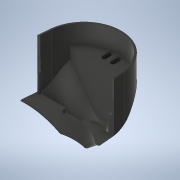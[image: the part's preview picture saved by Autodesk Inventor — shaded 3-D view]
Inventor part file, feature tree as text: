
AUTODESK INVENTOR PART (.ipt)
format: ipt  version: 2020.1 (Build 241239000, 239)  size: 3,823,104 bytes
history: native  units: mm
features: other x23, sketch x21, surface_op x16, extrude x11, projected_geometry x7, fillet x6, plane x4, emboss x3, delete_face x1, shell x1, loft x1
ambient origin geometry x8: Origin, YZ Plane, XZ Plane, XY Plane, X Axis, Y Axis, Z Axis, Center Point
bodies: Solid9 (feature_tree)
feature tree (94):
  other  "Bash Guard.ipt"
  sketch  "Sketch18"  dims[d14=2.75mm d15=2.75mm d26=64.0mm d170=52.0mm d171=2.0mm]
  plane  "Work Plane7"
  sketch  "Sketch19"  dims[d276=10.0mm d277=2.75mm d278=18.0mm]
  sketch  "Sketch20"  dims[d279=2.75mm d280=3.5mm]
  sketch  "3D Sketch6"
  plane  "Work Plane8"
  sketch  "Sketch21"  dims[d281=21.512mm d282=7.0mm]
  sketch  "Sketch22"  dims[d286=42.0mm d289=10.0mm]
  delete_face  "Delete Face7"
  sketch  "Sketch23"  dims[d290=0.0mm d291=0.0mm]
  surface_op  "Stitch Surface4"
  surface_op  "Stitch Surface5"
  surface_op  "Trim3"
  surface_op  "Trim4"
  surface_op  "Trim5"
  surface_op  "Extend2"
  surface_op  "Trim6"
  surface_op  "Extend3"
  surface_op  "Sculpt2"
  fillet  "Fillet7"  Radius=52.0mm
  sketch  "Sketch28"  dims[d299=2.75mm d300=17.0mm d301=2.0mm]
  extrude  "Extrusion19"  Depth=2.75mm
  shell  "Shell2"  Thickness=18.0mm
  extrude  "Extrusion20"  Depth=3.5mm
  extrude  "Extrusion21"  Depth=7.0mm
  extrude  "Extrusion22"  Depth=10.0mm
  extrude  "Extrusion23"  TaperAngle=0.0deg  [1 undecoded]
  extrude  "Extrusion24"  Depth=2.0mm
  fillet  "Fillet8"  Radius=2.75mm
  fillet  "Fillet9"  Radius=1.0mm
  extrude  "Extrusion25"  [1 undecoded]
  emboss  "Emboss1"
  plane  "Work Plane9"
  other  "Form7"
  surface_op  "Extend5"
  surface_op  "Sculpt4"
  extrude  "Extrusion26"  Depth=17.0mm
  fillet  "Fillet10"  Radius=2.0mm
  plane  "Work Plane10"
  sketch  "Sketch38"  dims[d331=4.25mm]
  extrude  "Extrusion27"  Depth=2.0mm
  fillet  "Fillet11"  [1 undecoded]
  fillet  "Fillet12"  [1 undecoded]
  emboss  "Emboss2"
  emboss  "Emboss3"
  other  "Holder::Bash Guard.ipt"
  other  "Holder Cover::Bash Guard.ipt"
  other  "TaggingFeature2"
  other  "3D Intersection1"
  other  "3D Intersection2"
  sketch  "3D Sketch7"
  other  "Srf7"
  other  "Srf8"
  other  "Srf11"
  sketch  "Sketch24"  dims[d292=-24.0mm d293=2.0mm d294=2.75mm d296=1.0mm]
  other  "Srf12"
  sketch  "3D Sketch8"
  other  "3D Intersection3"
  other  "Srf13"
  other  "Form6"
  surface_op  "Stitch Surface2"
  other  "Srf15"
  surface_op  "Stitch Surface3"
  other  "Srf16"
  other  "Srf17"
  other  "Srf18"
  sketch  "Sketch27"  dims[d297=2.0mm d298=-42.0mm]
  other  "Srf19"
  other  "Motor Cap"
  sketch  "Sketch29"  dims[d302=2.0mm d303=2.0mm d310=0.0mm d311=90.0deg d312=0.0mm d313=90.0deg]
  sketch  "Sketch30"  dims[d314=0.0mm d315=90.0deg d316=0.0mm d317=90.0deg]
  sketch  "Sketch31"  dims[d318=0.0mm d319=90.0deg d320=28.295mm d321=0.0mm]
  projected_geometry  "Projected Loop7"
  projected_geometry  "Projected Loop8"
  projected_geometry  "Projected Loop9"
  sketch  "Sketch35"  dims[d322=0.0mm d327=20.0mm d328=0.0mm]
  sketch  "Sketch36"  dims[d329=42.0mm]
  sketch  "Sketch37"  dims[d330=4.5mm]
  sketch  "Sketch39"  dims[d332=2.0mm]
  sketch  "Sketch40"  dims[d333=20.0mm d334=0.0mm d335=1.5mm d336=1.5mm d337=55.0mm d338=0.0mm d339=15.37mm d340=0.0mm d341=15.37mm d342=0.0mm d343=15.37mm d344=0.0mm d347=15.0mm d348=0.0mm d351=7.0mm d352=2.0mm d353=1.0mm d354=0.5mm d361=18.397mm d362=0.0mm d363=0.8mm d364=0.0mm d365=3.5mm d366=10.0mm d367=3.2mm d368=29.663794mm d369=3.0mm d371=3.0mm d372=0.0mm d374=15.0mm d375=2.0mm d376=0.4mm d377=0.0mm d378=0.4mm d379=0.0mm d380=3.5mm d381=9.0mm d382=0.0mm d383=1.25mm d384=1.25mm]
  projected_geometry  "Projected Loop12"
  projected_geometry  "Projected Loop13"
  projected_geometry  "Projected Loop14"
  projected_geometry  "Projected Loop15"
  loft  "LoftSrf1"
  extrude  "ExtrusionSrf2"  Depth=28.295mm TaperAngle=0.0deg
  extrude  "ExtrusionSrf3"  Depth=20.0mm TaperAngle=0.0deg
  surface_op  "Boundary Patch5"
  other  "Srf14"
  other  "Srf23"
  surface_op  "Boundary Patch3"
  surface_op  "Boundary Patch4"
  other  "Holder"
note: 4 required parameter values undecoded (feature->parameter linkage not recoverable at this tier; creation-order binding heuristic only, values carry confidence <= 0.55)
